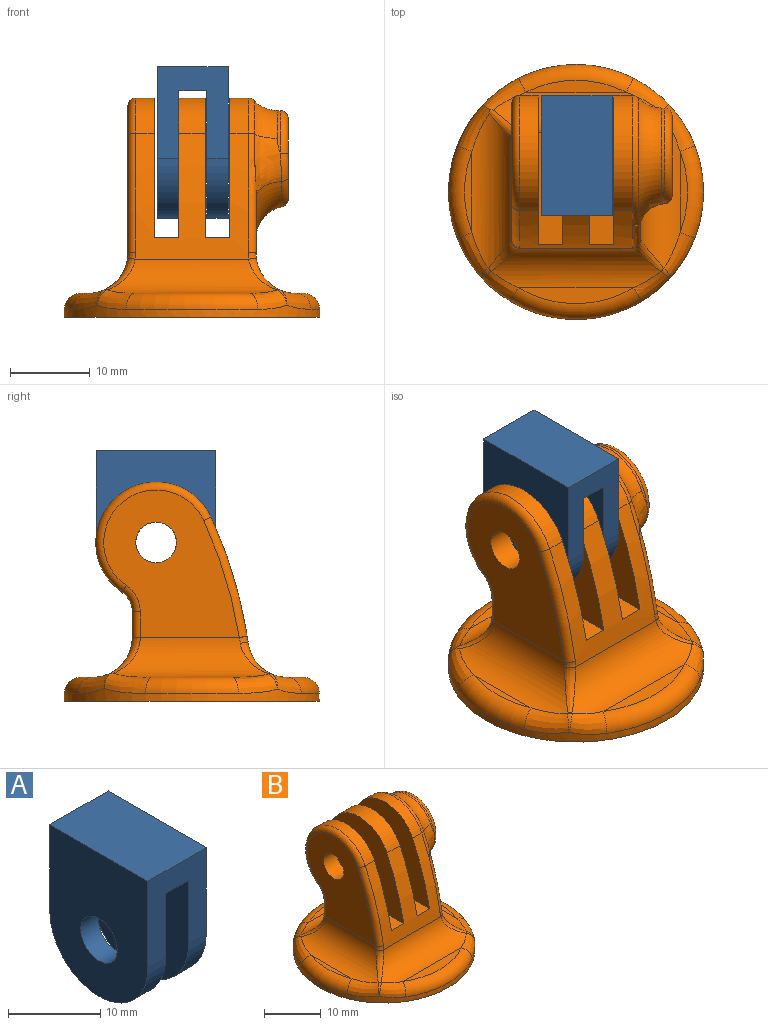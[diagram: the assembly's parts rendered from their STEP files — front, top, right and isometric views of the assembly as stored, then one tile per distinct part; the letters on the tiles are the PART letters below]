
ASSEMBLY  parts=2 mates=1
PART A: 12 faces, bbox 8.9x15x19 mm
  f0: cylinder r=7.5mm len=15mm, axis (-1,0,0), area 63.6mm2, adj f1,f3,f4,f5
  f1: plane 11.5x8.9mm, normal (0,1,0), area 72.6mm2, adj f0,f4,f5,f6,f7,f9,f10,f11
  f2: cylinder r=2.8mm len=5.6mm, axis (-1,0,0), area 47.5mm2, adj f4,f5
  f3: plane 11.5x8.9mm, normal (0,-1,0), area 72.6mm2, adj f0,f4,f5,f6,f7,f9,f10,f11
  f4: plane 16x15mm, normal (1,0,0), area 191.2mm2, adj f0,f1,f2,f3,f6
  f5: plane 19x15mm, normal (-1,0,0), area 236.2mm2, adj f0,f1,f2,f3,f11
  f6: plane 15x3.5mm, normal (0,0,-1), area 52.5mm2, adj f1,f3,f4,f10
  f7: cylinder r=7.5mm len=15mm, axis (-1,0,0), area 63.6mm2, adj f1,f3,f9,f10
  f8: cylinder r=2.8mm len=5.6mm, axis (-1,0,0), area 47.5mm2, adj f9,f10
  f9: plane 19x15mm, normal (1,0,0), area 236.2mm2, adj f1,f3,f7,f8,f11
  f10: plane 16x15mm, normal (-1,0,0), area 191.2mm2, adj f1,f3,f6,f7,f8
  f11: plane 15x8.9mm, normal (0,0,1), area 133.5mm2, adj f1,f3,f5,f9
PART B: 92 faces, bbox 34.6x34.6x30.7 mm
  f0: plane 4.16x2.4mm, normal (1,0,0), area 1.9mm2, adj f80,f91
  f1: plane 3.97x2.29mm, normal (1,0,0), area 1.6mm2, adj f78,f87,f88,f90,f91
  f2: plane 4.36x0.5mm, normal (1,0,0), area 1.5mm2, adj f76,f87
  f3: plane 3.78x2.18mm, normal (1,0,0), area 1.5mm2, adj f77,f87
  f4: plane 3.78x2.18mm, normal (1,0,0), area 1.5mm2, adj f79,f87
  f5: plane 14.42x2mm, normal (0,0,1), area 19.5mm2, adj f32,f41
  f6: plane 12.61x1.5mm, normal (0,0,1), area 12.8mm2, adj f29,f36
  f7: plane 10.14x0.95mm, normal (0,0,1), area 6.5mm2, adj f30,f35
  f8: cylinder r=4.05mm len=8.1mm, axis (0,0,-1), area 146.3mm2, adj f9,f63
  f9: plane 8.1x8.1mm, normal (0,0,-1), area 51.5mm2, adj f8
  f10: cylinder r=16mm len=32mm, axis (0,0,-1), area 113.2mm2, adj f12,f33,f34,f35,f36,f37,f38,f39
  f11: plane 10.14x0.95mm, normal (0,0,1), area 6.5mm2, adj f31,f42
  f12: plane 32x32mm, normal (0,0,-1), area 724.1mm2, adj f10,f63
  f13: plane 14.1x3.1mm, normal (0,0,1), area 43.7mm2, adj f15,f16,f21,f25
  f14: plane 14.1x3.1mm, normal (0,0,1), area 43.7mm2, adj f15,f16,f22,f28
  f15: cylinder r=56.97mm len=15.81mm, axis (-1,0,0), area 147.8mm2, adj f13,f14,f20,f21,f22,f24,f25,f26
  f16: plane 14.1x3.22mm, normal (0,1,0), area 37.8mm2, adj f13,f14,f19,f21,f22,f23,f25,f27
  f17: plane 12.43x7.18mm, normal (1,0,0), area 40.7mm2, adj f31,f55,f58,f84
  f18: plane 18.5x17.01mm, normal (-1,0,0), area 201.4mm2, adj f30,f46,f47,f48,f49,f64
  f19: cylinder r=3mm len=3.3mm, axis (-1,0,0), area 9.6mm2, adj f16,f20,f21,f22
  f20: cylinder r=7.58mm len=14.45mm, axis (-1,0,0), area 91.9mm2, adj f15,f19,f21,f22
  f21: plane 18.67x17.5mm, normal (1,0,0), area 221.1mm2, adj f13,f15,f16,f19,f20,f66
  f22: plane 18.67x17.5mm, normal (-1,0,0), area 221.1mm2, adj f14,f15,f16,f19,f20,f66
  f23: cylinder r=3mm len=2.47mm, axis (-1,0,0), area 6.7mm2, adj f16,f24,f25,f56
  f24: cylinder r=7.58mm len=14.45mm, axis (-1,0,0), area 64.1mm2, adj f15,f23,f25,f57
  f25: plane 18.67x17.5mm, normal (-1,0,0), area 221.1mm2, adj f13,f15,f16,f23,f24,f65
  f26: cylinder r=7.58mm len=14.45mm, axis (-1,0,0), area 64.1mm2, adj f15,f27,f28,f48
  f27: cylinder r=3mm len=2.47mm, axis (-1,0,0), area 6.7mm2, adj f16,f26,f28,f47
  f28: plane 18.67x17.5mm, normal (1,0,0), area 221.1mm2, adj f14,f15,f16,f26,f27,f64
  f29: cylinder r=5mm len=20.77mm, axis (-1,0,0), area 135.2mm2, adj f6,f16,f34,f38,f45,f54
  f30: cylinder r=5mm len=19.42mm, axis (0,-1,0), area 118.4mm2, adj f7,f18,f33,f37,f45,f50,f51,f52
  f31: cylinder r=5mm len=19.42mm, axis (0,1,0), area 118.4mm2, adj f11,f17,f40,f44,f54,f59,f60,f61
  f32: cylinder r=5mm len=21.2mm, axis (-1,0,0), area 126.7mm2, adj f5,f15,f39,f43,f51,f60
  f33: bspline ~8.4x5.11mm, area 16.9mm2, adj f10,f30,f34,f35,f45
  f34: bspline ~7.92x5.42mm, area 15.1mm2, adj f10,f29,f33,f36,f45
  f35: torus R=14mm, axis (0,0,1), area 35.6mm2, adj f7,f10,f33,f37
  f36: torus R=14mm, axis (0,0,1), area 44.8mm2, adj f6,f10,f34,f38
  f37: bspline ~8.11x4.92mm, area 15.5mm2, adj f10,f30,f35,f53
  f38: bspline ~7.92x5.42mm, area 15.1mm2, adj f10,f29,f36,f40,f54
  f39: bspline ~6.75x4.95mm, area 12.7mm2, adj f10,f32,f41,f52,f53
  f40: bspline ~8.4x5.11mm, area 16.9mm2, adj f10,f31,f38,f42,f54
  f41: torus R=14mm, axis (0,0,1), area 51.9mm2, adj f5,f10,f39,f43
  f42: torus R=14mm, axis (0,0,1), area 35.6mm2, adj f10,f11,f40,f44
  f43: bspline ~6.75x4.95mm, area 12.7mm2, adj f10,f32,f41,f61,f62
  f44: bspline ~8.11x4.92mm, area 15.5mm2, adj f10,f31,f42,f62
  f45: bspline ~5.34x4.24mm, area 7.8mm2, adj f29,f30,f33,f34,f46
  f46: cylinder r=1mm len=3.22mm, axis (0,0,-1), area 5.1mm2, adj f16,f18,f45,f47
  f47: torus R=4mm, axis (-1,0,0), area 5.1mm2, adj f18,f27,f46,f48
  f48: torus R=6.58mm, axis (-1,0,0), area 41.6mm2, adj f18,f26,f47,f49
  f49: torus R=55.97mm, axis (-1,0,0), area 24.5mm2, adj f15,f18,f48,f50
  f50: bspline ~2.54x1.35mm, area 1.2mm2, adj f15,f30,f49,f51
  f51: bspline ~4.42x4.23mm, area 6.8mm2, adj f30,f32,f50,f52
  f52: bspline ~0.52x0.5mm, area 0mm2, adj f30,f39,f51,f53
  f53: bspline ~2.09x1.59mm, area 0.5mm2, adj f37,f39,f52
  f54: bspline ~5.34x4.24mm, area 7.8mm2, adj f29,f31,f38,f40,f55
  f55: cylinder r=1mm len=3.22mm, axis (0,0,1), area 4.7mm2, adj f16,f17,f54,f56,f86
  f56: torus R=4mm, axis (-1,0,0), area 2.6mm2, adj f23,f55,f57,f85
  f57: torus R=6.58mm, axis (-1,0,0), area 22.4mm2, adj f24,f56,f58,f83
  f58: torus R=55.97mm, axis (-1,0,0), area 21.4mm2, adj f15,f17,f57,f59,f82
  f59: bspline ~2.54x1.35mm, area 1.2mm2, adj f15,f31,f58,f60
  f60: bspline ~4.42x4.23mm, area 6.8mm2, adj f31,f32,f59,f61
  f61: bspline ~0.55x0.55mm, area 0mm2, adj f31,f43,f60,f62
  f62: bspline ~2.09x1.59mm, area 0.5mm2, adj f43,f44,f61
  f63: torus R=5.05mm, axis (0,0,1), area 43.6mm2, adj f8,f12
  f64: cylinder r=2.55mm len=5.1mm, axis (1,0,0), area 52.9mm2, adj f18,f28
  f65: cylinder r=2.55mm len=5.1mm, axis (1,0,0), area 52.9mm2, adj f25,f69
  f66: cylinder r=2.55mm len=5.1mm, axis (1,0,0), area 52.9mm2, adj f21,f22
  f67: cylinder r=6mm len=11.96mm, axis (-1,0,0), area 8.3mm2, adj f82,f83,f85,f87
  f68: plane 4.58x0.51mm, normal (1,0,0), area 1.6mm2, adj f81,f87,f89
  f69: plane 9.24x8mm, normal (1,0,0), area 35mm2, adj f65,f70,f71,f72,f73,f74,f75
  f70: plane 4x3.5mm, normal (0,-0.5,0.87), area 16.2mm2, adj f69,f71,f75,f78
  f71: plane 4.62x3.5mm, normal (0,-1,0), area 16.2mm2, adj f69,f70,f72,f76
  f72: plane 4x3.5mm, normal (0,-0.5,-0.87), area 16.2mm2, adj f69,f71,f73,f77
  f73: plane 4x3.5mm, normal (0,0.5,-0.87), area 16.2mm2, adj f69,f72,f74,f79
  f74: plane 4.62x3.5mm, normal (0,1,0), area 16.2mm2, adj f69,f73,f75,f81
  f75: plane 4x3.5mm, normal (0,0.5,0.87), area 16.2mm2, adj f69,f70,f74,f80
  f76: cylinder r=0.5mm len=5.11mm, axis (0,0,-1), area 3.8mm2, adj f2,f71,f77,f78,f87
  f77: cylinder r=0.5mm len=4.67mm, axis (0,0.87,-0.5), area 3.8mm2, adj f3,f72,f76,f79,f87
  f78: cylinder r=0.5mm len=4.69mm, axis (0,-0.87,-0.5), area 3.8mm2, adj f1,f70,f76,f80,f87,f91
  f79: cylinder r=0.5mm len=4.67mm, axis (0,0.87,0.5), area 3.8mm2, adj f4,f73,f77,f81,f87
  f80: cylinder r=0.5mm len=4.71mm, axis (0,-0.87,0.5), area 3.8mm2, adj f0,f75,f78,f81,f91
  f81: cylinder r=0.5mm len=5.13mm, axis (0,0,1), area 3.8mm2, adj f68,f74,f79,f80,f87,f89,f91
  f82: bspline ~9.09x4.56mm, area 26.2mm2, adj f58,f67,f83,f84,f89
  f83: torus R=10mm, axis (1,0,0), area 77.2mm2, adj f57,f67,f82,f85
  f84: torus R=10mm, axis (-1,0,0), area 53.6mm2, adj f17,f82,f86,f91
  f85: bspline ~4.56x3.69mm, area 6.5mm2, adj f56,f67,f83,f86,f88
  f86: bspline ~4.78x4.24mm, area 5.8mm2, adj f55,f84,f85,f90
  f87: torus R=5mm, axis (1,0,0), area 35.9mm2, adj f1,f2,f3,f4,f67,f68,f76,f77
  f88: bspline ~1.16x1.03mm, area 0.1mm2, adj f1,f85,f87,f90
  f89: bspline ~5.04x1.6mm, area 5mm2, adj f68,f81,f82,f87,f91
  f90: bspline ~2.77x2.03mm, area 2.5mm2, adj f1,f86,f88,f91
  f91: torus R=5.1mm, axis (-1,0,0), area 9.9mm2, adj f0,f1,f78,f80,f81,f84,f89,f90
PLACE A t=(-4.21,-0.97,-2.67)mm
PLACE B t=(0.14,-5.47,-22.59)mm
MATE fastened B.f20 <-> A.f2  axis (-1,0,0) through (-1.51,-0.97,-2.67)mm
